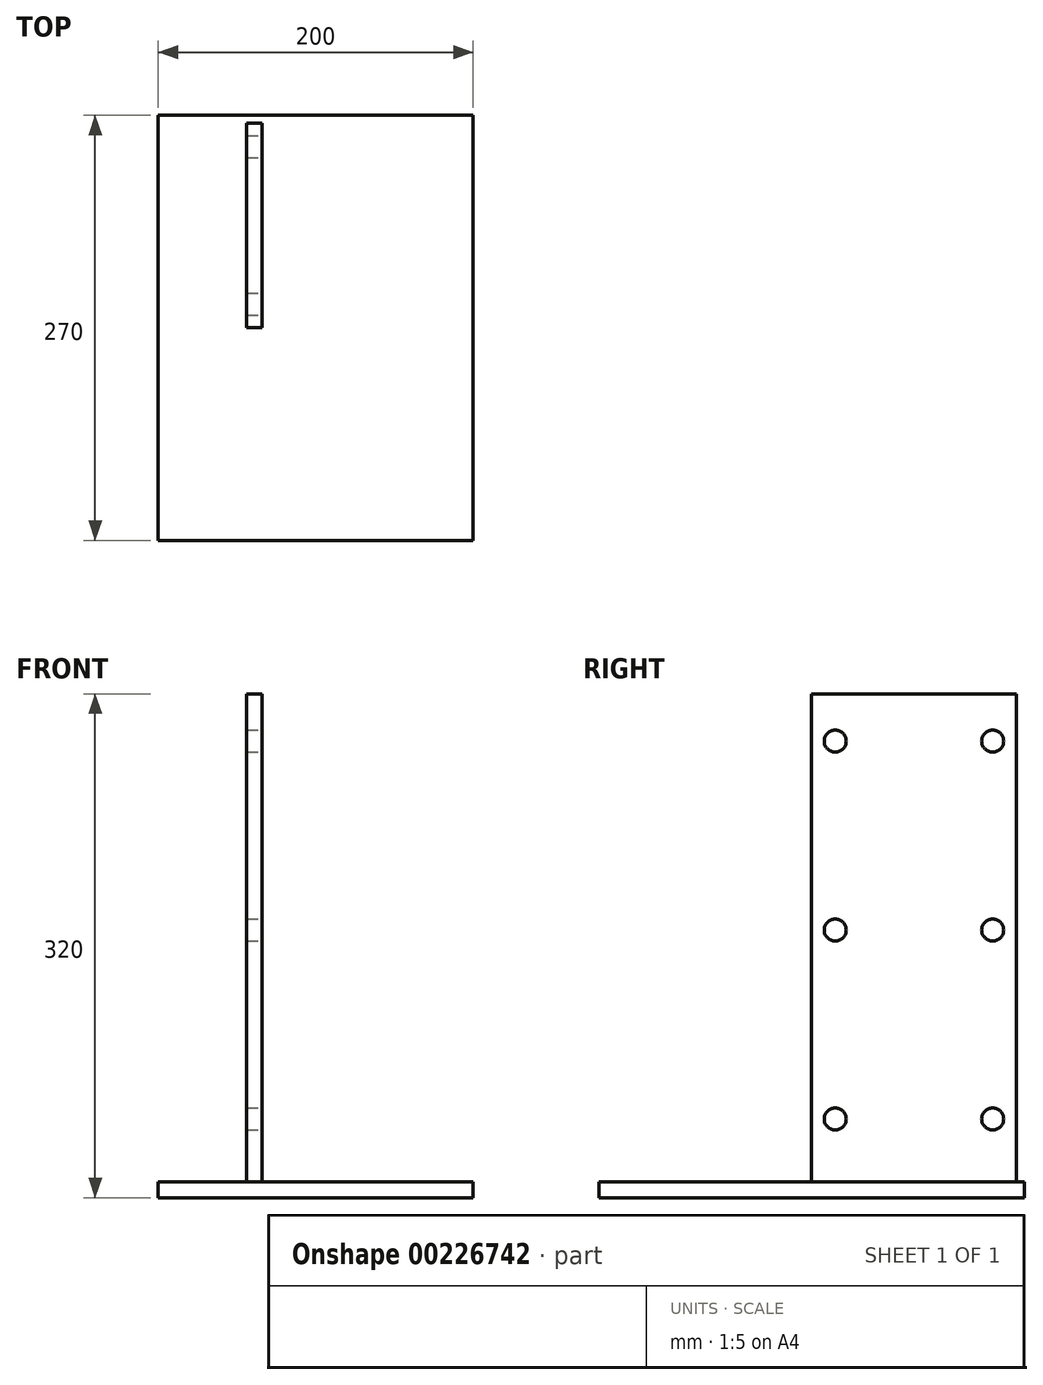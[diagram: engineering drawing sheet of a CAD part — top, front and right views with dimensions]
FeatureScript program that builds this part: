
annotation { "Feature Type Name" : "Feature", "Feature Type Description" : "" }
export const myFeature = defineFeature(function(context is Context, id is Id, definition is map)
    precondition{}
    {
        {
            var Q0;
            Q0=qCreatedBy(makeId("Top.planeOp"),FACE);
            var sketch = newSketch(context, id + "F0", { "sketchPlane" : qUnion([Q0])});
            skLineSegment(sketch, "E0.bottom", {"start": v(0.07, 0) * mm, "end": v(200.07, 0) * mm});
            skLineSegment(sketch, "E0.top", {"start": v(0.07, 270) * mm, "end": v(200.07, 270) * mm});
            skLineSegment(sketch, "E0.left", {"start": v(0.07, 0) * mm, "end": v(0.07, 270) * mm});
            skLineSegment(sketch, "E0.right", {"start": v(200.07, 0) * mm, "end": v(200.07, 270) * mm});
            skSolve(sketch);
        }
        {
            var Q0;
            Q0=makeQuery(id+"F0.imprint","IMPRINT",FACE,{"disambiguationData":[TD([[makeQuery(id+"F0.imprint","IMPRINT",EDGE,{"derivedFrom":sQuery(id+"F0.wireOp",EDGE,"E0.bottom")}),1.0]])]});
            extrude(context, id + "F1", {"entities" : qUnion([Q0]), "depth" : 10 * mm});
        }
        {
            var Q0;
            Q0=makeQuery(id+"F1.opExtrude","CAP_FACE",FACE,{"disambiguationData":[OSD([sQuery(id+"F0.wireOp",EDGE,"E0.bottom"),sQuery(id+"F0.wireOp",EDGE,"E0.top"),sQuery(id+"F0.wireOp",EDGE,"E0.left"),sQuery(id+"F0.wireOp",EDGE,"E0.right")])],"isStart":false});
            var sketch = newSketch(context, id + "F2", { "sketchPlane" : qUnion([Q0])});
            skLineSegment(sketch, "E1.bottom", {"start": v(56.07, 265) * mm, "end": v(66.07, 265) * mm});
            skLineSegment(sketch, "E1.top", {"start": v(56.07, 135) * mm, "end": v(66.07, 135) * mm});
            skLineSegment(sketch, "E1.left", {"start": v(56.07, 265) * mm, "end": v(56.07, 135) * mm});
            skLineSegment(sketch, "E1.right", {"start": v(66.07, 265) * mm, "end": v(66.07, 135) * mm});
            skSolve(sketch);
        }
        {
            var Q0;
            Q0 = qSketchRegion(id + "F2", true);
            extrude(context, id + "F3", {"entities" : qUnion([Q0]), "operationType" : NewBodyOperationType.ADD, "depth" : 310 * mm});
        }
        {
            var Q0;
            Q0=makeQuery(id+"F3.opExtrude","SWEPT_FACE",FACE,{"disambiguationData":[OSD([sQuery(id+"F2.wireOp",EDGE,"E1.right")])]});
            var sketch = newSketch(context, id + "F4", { "sketchPlane" : qUnion([Q0])});
            skPoint(sketch, "E2", {"position": v(150, 50) * mm});
            skPoint(sketch, "E3", {"position": v(250, 50) * mm});
            skPoint(sketch, "E4", {"position": v(150, 170) * mm});
            skPoint(sketch, "E5", {"position": v(250, 170) * mm});
            skPoint(sketch, "E6", {"position": v(150, 290) * mm});
            skPoint(sketch, "E7", {"position": v(250, 290) * mm});
            skSolve(sketch);
        }
        {
            var Q0;
            Q0=sQuery(id+"F4.wireOp",VERTEX,"E4");
            var Q1;
            Q1=sQuery(id+"F4.wireOp",VERTEX,"E2");
            var Q2;
            Q2=sQuery(id+"F4.wireOp",VERTEX,"E3");
            var Q3;
            Q3=sQuery(id+"F4.wireOp",VERTEX,"E5");
            var Q4;
            Q4=sQuery(id+"F4.wireOp",VERTEX,"E7");
            var Q5;
            Q5=sQuery(id+"F4.wireOp",VERTEX,"E6");
            var Q6;
            Q6=makeQuery(id+"F1.opExtrude","SWEPT_BODY",BODY,{"disambiguationData":[OSD([sQuery(id+"F0.wireOp",EDGE,"E0.bottom"),sQuery(id+"F0.wireOp",EDGE,"E0.top"),sQuery(id+"F0.wireOp",EDGE,"E0.left"),sQuery(id+"F0.wireOp",EDGE,"E0.right")])]});
            hole(context, id + "F5", {"style" : HoleStyle.SIMPLE, "endStyle" : HoleEndStyle.THROUGH, "holeDiameter" : 14 * mm, "locations" : qUnion([Q0, Q1, Q2, Q3, Q4, Q5]), "scope" : qUnion([Q6]), "isTappedThrough" : true});
        }
    });
